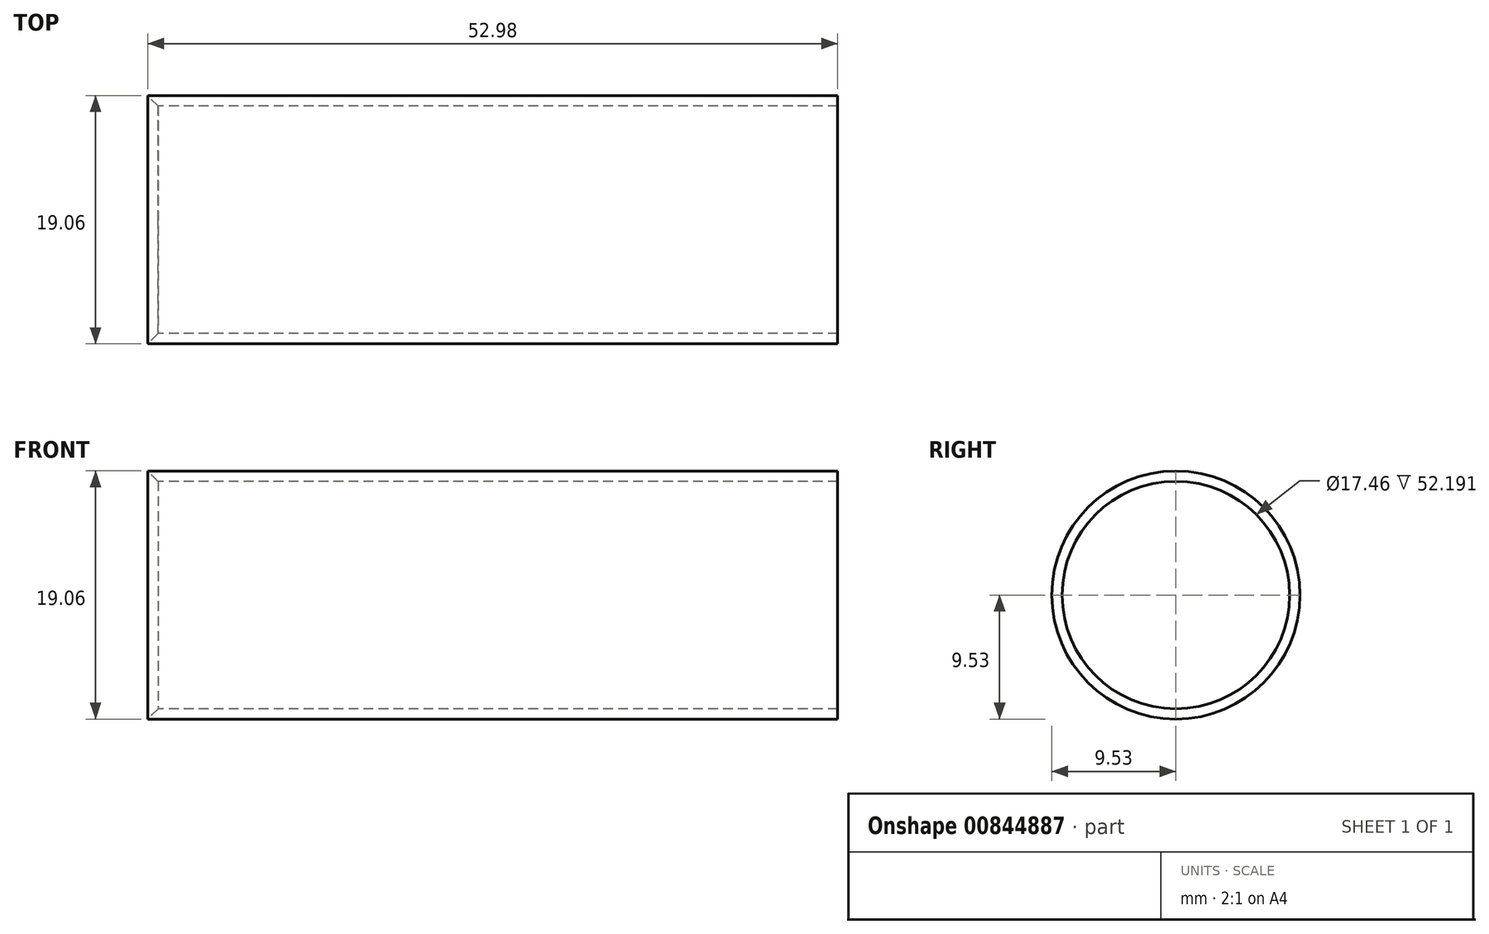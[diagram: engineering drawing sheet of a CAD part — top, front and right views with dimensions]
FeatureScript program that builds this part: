
annotation { "Feature Type Name" : "Feature", "Feature Type Description" : "" }
export const myFeature = defineFeature(function(context is Context, id is Id, definition is map)
    precondition{}
    {
        {
            var Q0;
            Q0=qCreatedBy(makeId("Front.planeOp"),FACE);
            var sketch = newSketch(context, id + "F0", { "sketchPlane" : qUnion([Q0])});
            skLineSegment(sketch, "E0.bottom", {"start": v(0.8, 8.73) * mm, "end": v(52.98, 8.73) * mm});
            skLineSegment(sketch, "E0.top", {"start": v(0, 9.53) * mm, "end": v(52.98, 9.53) * mm});
            skLineSegment(sketch, "E0.right", {"start": v(52.98, 8.73) * mm, "end": v(52.98, 9.53) * mm});
            skLineSegment(sketch, "E1", {"start": v(0, 0) * mm, "end": v(54.15, 0) * mm, "construction": true});
            skLineSegment(sketch, "E2", {"start": v(0, 9.53) * mm, "end": v(0.8, 8.73) * mm});
            skPoint(sketch, "E3.orphan", {"position": v(0, 8.73) * mm});
            skSolve(sketch);
        }
        {
            var Q0;
            Q0 = qSketchRegion(id + "F0", true);
            var Q1;
            Q1=makeQuery(id+"F0.imprint","IMPRINT",FACE,{"disambiguationData":[TD([[makeQuery(id+"F0.imprint","IMPRINT",EDGE,{"derivedFrom":sQuery(id+"F0.wireOp",EDGE,"E0.bottom")}),1.0]])]});
            var Q2;
            Q2=sQuery(id+"F0.wireOp",EDGE,"E1");
            revolve(context, id + "F1", {"surfaceOperationType" : NewSurfaceOperationType.NEW, "entities" : qUnion([Q0, Q1]), "axis" : qUnion([Q2]), "revolveType" : RevolveType.FULL});
        }
    });
